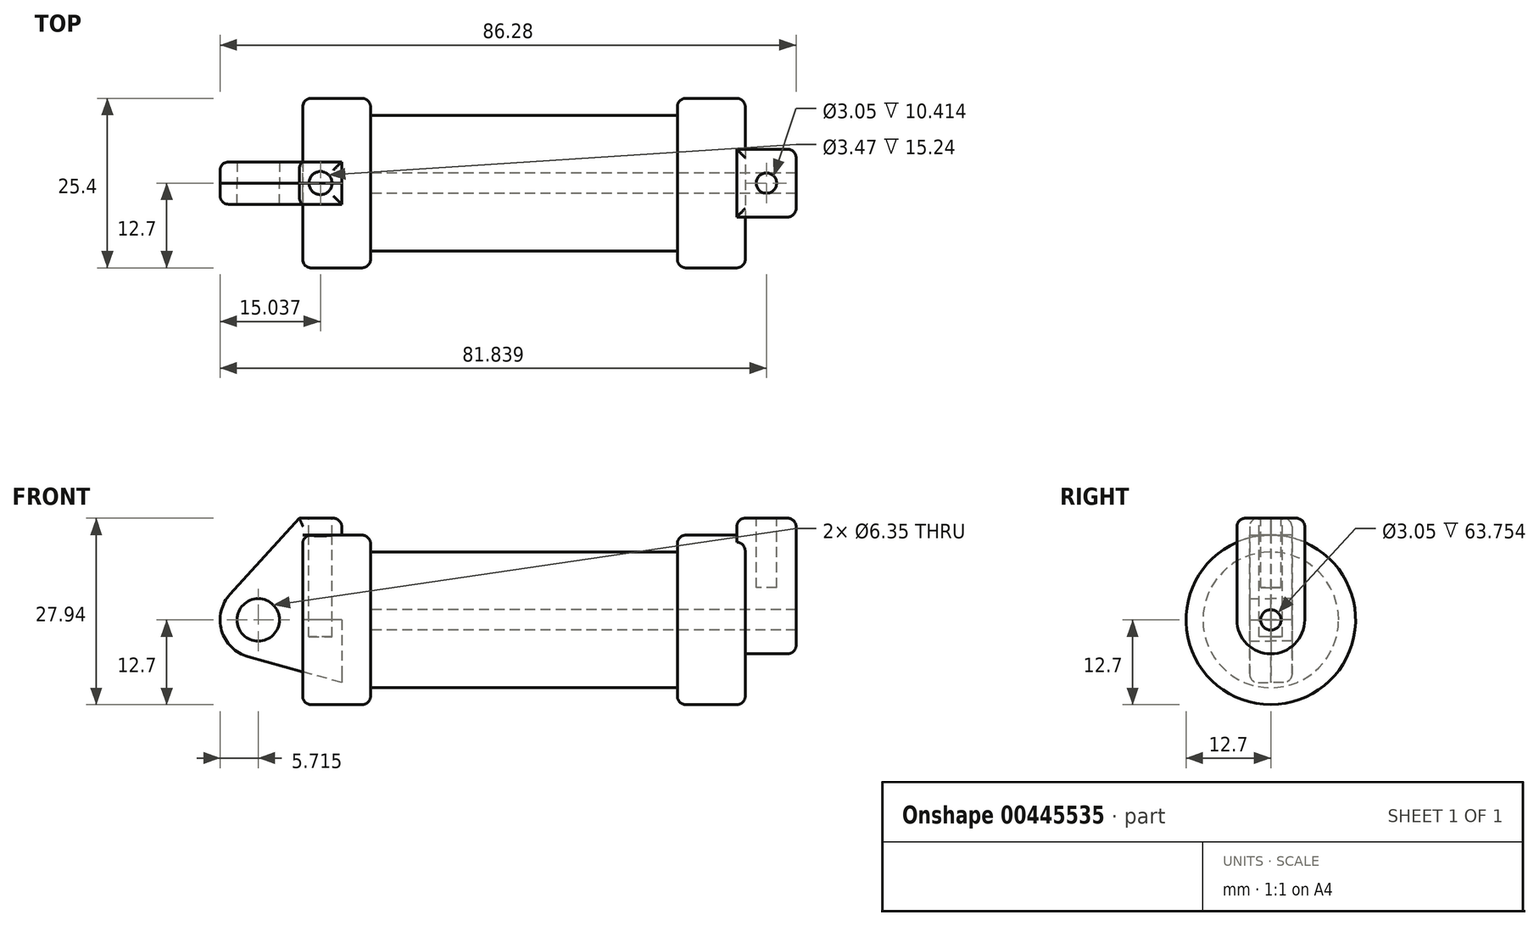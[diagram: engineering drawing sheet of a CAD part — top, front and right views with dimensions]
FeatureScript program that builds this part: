
annotation { "Feature Type Name" : "Feature", "Feature Type Description" : "" }
export const myFeature = defineFeature(function(context is Context, id is Id, definition is map)
    precondition{}
    {
        {
            var Q0;
            Q0=qCreatedBy(makeId("Front.planeOp"),FACE);
            var sketch = newSketch(context, id + "F0", { "sketchPlane" : qUnion([Q0])});
            skLineSegment(sketch, "E0", {"start": v(0, 0) * mm, "end": v(0, 12.7) * mm});
            skLineSegment(sketch, "E1", {"start": v(0, 12.7) * mm, "end": v(10.16, 12.7) * mm});
            skLineSegment(sketch, "E2", {"start": v(10.16, 12.7) * mm, "end": v(10.16, 10.16) * mm});
            skLineSegment(sketch, "E3", {"start": v(10.16, 10.16) * mm, "end": v(56.13, 10.16) * mm});
            skLineSegment(sketch, "E4", {"start": v(56.13, 10.16) * mm, "end": v(56.13, 12.7) * mm});
            skLineSegment(sketch, "E5", {"start": v(56.13, 12.7) * mm, "end": v(66.3, 12.7) * mm});
            skLineSegment(sketch, "E6", {"start": v(66.3, 12.7) * mm, "end": v(66.3, 0) * mm});
            skLineSegment(sketch, "E7", {"start": v(66.3, 0) * mm, "end": v(0, 0) * mm});
            skLineSegment(sketch, "E8", {"start": v(5.84, 15.24) * mm, "end": v(-0.5, 15.24) * mm});
            skLineSegment(sketch, "E9", {"start": v(-0.5, 15.24) * mm, "end": v(-10.88, 3.85) * mm});
            skLineSegment(sketch, "E10", {"start": v(0, 0) * mm, "end": v(-6.65, 0) * mm});
            skCircle(sketch, "E11", {"center": v(-6.65, 0) * mm, "radius": 5.72 * mm});
            skCircle(sketch, "E12", {"center": v(-6.65, 0) * mm, "radius": 3.18 * mm});
            skLineSegment(sketch, "E13", {"start": v(5.84, 15.24) * mm, "end": v(5.84, -9.4) * mm});
            skLineSegment(sketch, "E14", {"start": v(5.84, -9.4) * mm, "end": v(-8.18, -5.5) * mm});
            skSolve(sketch);
        }
        {
            var Q0;
            {var subQ0=sQuery(id+"F0.wireOp",EDGE,"E0");Q0=makeQuery(id+"F0.imprint","IMPRINT",FACE,{"disambiguationData":[TD([[makeQuery(id+"F0.imprint","IMPRINT",EDGE,{"derivedFrom":subQ0}),-1.0]])]});}
            var Q1;
            Q1=sQuery(id+"F0.wireOp",EDGE,"E7");
            revolve(context, id + "F1", {"entities" : qUnion([Q0]), "axis" : qUnion([Q1]), "revolveType" : RevolveType.FULL});
        }
        {
            var Q0;
            {var subQ0=sQuery(id+"F0.wireOp",EDGE,"E2");Q0=makeQuery(id+"F0.imprint","IMPRINT",FACE,{"disambiguationData":[TD([[makeQuery(id+"F0.imprint","IMPRINT",EDGE,{"derivedFrom":subQ0}),-1.0]])]});}
            var Q1;
            Q1=sQuery(id+"F0.wireOp",EDGE,"E7");
            revolve(context, id + "F2", {"operationType" : NewBodyOperationType.ADD, "entities" : qUnion([Q0]), "axis" : qUnion([Q1]), "revolveType" : RevolveType.FULL});
        }
        {
            var Q0;
            {var subQ5=sQuery(id+"F0.wireOp",EDGE,"E12");Q0=makeQuery(id+"F0.imprint","IMPRINT",FACE,{"disambiguationData":[TD([[makeQuery(id+"F0.imprint","IMPRINT",EDGE,{"derivedFrom":subQ5}),-1.0]])]});}
            var Q1;
            {var subQ0=sQuery(id+"F0.wireOp",EDGE,"E14");Q1=makeQuery(id+"F0.imprint","IMPRINT",FACE,{"disambiguationData":[TD([[makeQuery(id+"F0.imprint","IMPRINT",EDGE,{"derivedFrom":subQ0}),-1.0]])]});}
            var Q2;
            {var subQ1=sQuery(id+"F0.wireOp",EDGE,"E0");Q2=makeQuery(id+"F0.imprint","IMPRINT",FACE,{"disambiguationData":[TD([[makeQuery(id+"F0.imprint","IMPRINT",EDGE,{"derivedFrom":subQ1}),1.0]])]});}
            extrude(context, id + "F3", {"entities" : qUnion([Q0, Q1, Q2]), "depth" : 3.17 * mm});
        }
        {
            var Q0;
            {var subQ1=sQuery(id+"F0.wireOp",EDGE,"E0");Q0=makeQuery(id+"F0.imprint","IMPRINT",FACE,{"disambiguationData":[TD([[makeQuery(id+"F0.imprint","IMPRINT",EDGE,{"derivedFrom":subQ1}),1.0]])]});}
            var Q1;
            {var subQ5=sQuery(id+"F0.wireOp",EDGE,"E12");Q1=makeQuery(id+"F0.imprint","IMPRINT",FACE,{"disambiguationData":[TD([[makeQuery(id+"F0.imprint","IMPRINT",EDGE,{"derivedFrom":subQ5}),-1.0]])]});}
            var Q2;
            {var subQ0=sQuery(id+"F0.wireOp",EDGE,"E14");Q2=makeQuery(id+"F0.imprint","IMPRINT",FACE,{"disambiguationData":[TD([[makeQuery(id+"F0.imprint","IMPRINT",EDGE,{"derivedFrom":subQ0}),-1.0]])]});}
            extrude(context, id + "F4", {"entities" : qUnion([Q0, Q1, Q2]), "oppositeDirection" : true, "depth" : 3.17 * mm});
        }
        {
            var Q0;
            Q0=makeQuery(id+"F2.opRevolve","SWEPT_FACE",FACE,{"disambiguationData":[OSD([sQuery(id+"F0.wireOp",EDGE,"E6")])]});
            var sketch = newSketch(context, id + "F5", { "sketchPlane" : qUnion([Q0])});
            skCircle(sketch, "E15", {"center": v(0, 0) * mm, "radius": 1.52 * mm});
            skCircle(sketch, "E16", {"center": v(0, 0) * mm, "radius": 5.08 * mm});
            skLineSegment(sketch, "E17", {"start": v(-5.08, 0) * mm, "end": v(-5.08, 15.24) * mm});
            skLineSegment(sketch, "E18", {"start": v(5.08, 0) * mm, "end": v(5.08, 15.24) * mm});
            skLineSegment(sketch, "E19", {"start": v(-5.08, 15.24) * mm, "end": v(-3.2, 15.24) * mm});
            skLineSegment(sketch, "E20", {"start": v(-3.2, 15.24) * mm, "end": v(5.08, 15.24) * mm});
            skSolve(sketch);
        }
        {
            var Q0;
            Q0=qSketchRegion(id+"F5",true);
            extrude(context, id + "F6", {"entities" : qUnion([Q0]), "operationType" : NewBodyOperationType.ADD, "depth" : 7.62 * mm});
        }
        {
            var Q0;
            Q0=qSketchRegion(id+"F5",true);
            var Q1;
            Q1=makeQuery(id+"F5.imprint","IMPRINT",FACE,{"disambiguationData":[TD([[makeQuery(id+"F5.imprint","IMPRINT",EDGE,{"derivedFrom":sQuery(id+"F5.wireOp",EDGE,"E15")}),1.0]])]});
            extrude(context, id + "F7", {"entities" : qUnion([Q0, Q1]), "operationType" : NewBodyOperationType.ADD, "oppositeDirection" : true, "depth" : 1.27 * mm});
        }
        {
            var Q0;
            Q0=makeQuery(id+"F6.boolean.opBoolean","SPLIT",FACE,{"disambiguationData":[TD([makeQuery(id+"F6.opExtrude","SWEPT_FACE",FACE,{"disambiguationData":[OSD([sQuery(id+"F5.wireOp",EDGE,"E15")])]})])],"derivedFrom":makeQuery(id+"F2.opRevolve","SWEPT_FACE",FACE,{"disambiguationData":[OSD([sQuery(id+"F0.wireOp",EDGE,"E6")])]})});
            var Q1;
            Q1=makeQuery(id+"F2.opRevolve","SWEPT_FACE",FACE,{"disambiguationData":[OSD([sQuery(id+"F0.wireOp",EDGE,"E2")])]});
            extrude(context, id + "F8", {"entities" : qUnion([Q0]), "operationType" : NewBodyOperationType.REMOVE, "endBound" : BoundingType.UP_TO_SURFACE, "oppositeDirection" : true, "endBoundEntityFace" : qUnion([Q1]), "depth" : 25.4 * mm});
        }
        {
            var Q0;
            {var subQ0=sQuery(id+"F5.wireOp",EDGE,"E20");var subQ1=sQuery(id+"F5.wireOp",EDGE,"E19");Q0=makeQuery(id+"F7.boolean.opBoolean","MERGE",FACE,{"derivedFrom":[makeQuery(id+"F6.opExtrude","SWEPT_FACE",FACE,{"disambiguationData":[OSD([subQ1,subQ0])]}),makeQuery(id+"F7.opExtrude","SWEPT_FACE",FACE,{"disambiguationData":[OSD([subQ1,subQ0])]})]});}
            var sketch = newSketch(context, id + "F9", { "sketchPlane" : qUnion([Q0])});
            skLineSegment(sketch, "E21", {"start": v(69.47, 5.08) * mm, "end": v(69.47, -5.08) * mm, "construction": true});
            skLineSegment(sketch, "E22", {"start": v(73.91, 0) * mm, "end": v(65.02, 0) * mm, "construction": true});
            skCircle(sketch, "E23", {"center": v(69.47, 0) * mm, "radius": 1.52 * mm});
            skSolve(sketch);
        }
        {
            var Q0;
            Q0=makeQuery(id+"F9.imprint","IMPRINT",FACE,{"disambiguationData":[TD([[makeQuery(id+"F9.imprint","IMPRINT",EDGE,{"derivedFrom":sQuery(id+"F9.wireOp",EDGE,"E23")}),1.0]])]});
            extrude(context, id + "F10", {"entities" : qUnion([Q0]), "operationType" : NewBodyOperationType.REMOVE, "oppositeDirection" : true, "depth" : 10.4 * mm});
        }
        {
            var Q0;
            Q0=makeQuery(id+"F4.opExtrude","SWEPT_FACE",FACE,{"disambiguationData":[OSD([sQuery(id+"F0.wireOp",EDGE,"E8")])]});
            var sketch = newSketch(context, id + "F11", { "sketchPlane" : qUnion([Q0])});
            skCircle(sketch, "E24", {"center": v(2.67, 0) * mm, "radius": 1.73 * mm});
            skSolve(sketch);
        }
        {
            var Q0;
            {var subQ0=sQuery(id+"F11.wireOp",EDGE,"E24");var subQ1=makeQuery(id+"F4.opExtrude","CAP_EDGE",EDGE,{"disambiguationData":[OSD([sQuery(id+"F0.wireOp",EDGE,"E8")])],"isStart":true});var subQ2=makeQuery(id+"F11.imprint","INTERSECT",VERTEX,{"disambiguationData":[OD(0.0)],"derivedFrom":[subQ1,subQ0]});Q0=makeQuery(id+"F11.imprint","IMPRINT",FACE,{"disambiguationData":[TD([[makeQuery(id+"F11.imprint","IMPRINT",EDGE,{"disambiguationData":[TD([[subQ2,-1.0]])],"derivedFrom":subQ0}),1.0]])]});}
            var Q1;
            {var subQ0=sQuery(id+"F11.wireOp",EDGE,"E24");var subQ1=makeQuery(id+"F4.opExtrude","CAP_EDGE",EDGE,{"disambiguationData":[OSD([sQuery(id+"F0.wireOp",EDGE,"E8")])],"isStart":true});var subQ2=makeQuery(id+"F11.imprint","INTERSECT",VERTEX,{"disambiguationData":[OD(0.0)],"derivedFrom":[subQ1,subQ0]});Q1=makeQuery(id+"F11.imprint","IMPRINT",FACE,{"disambiguationData":[TD([[makeQuery(id+"F11.imprint","IMPRINT",EDGE,{"disambiguationData":[TD([[subQ2,1.0]])],"derivedFrom":subQ0}),1.0]])]});}
            extrude(context, id + "F12", {"entities" : qUnion([Q0, Q1]), "operationType" : NewBodyOperationType.REMOVE, "oppositeDirection" : true, "depth" : 17.78 * mm});
        }
        {
            var Q0;
            {var subQ0=sQuery(id+"F11.wireOp",EDGE,"E24");var subQ1=makeQuery(id+"F4.opExtrude","CAP_EDGE",EDGE,{"disambiguationData":[OSD([sQuery(id+"F0.wireOp",EDGE,"E8")])],"isStart":true});var subQ2=makeQuery(id+"F11.imprint","INTERSECT",VERTEX,{"disambiguationData":[OD(0.0)],"derivedFrom":[subQ1,subQ0]});Q0=makeQuery(id+"F11.imprint","IMPRINT",FACE,{"disambiguationData":[TD([[makeQuery(id+"F11.imprint","IMPRINT",EDGE,{"disambiguationData":[TD([[subQ2,1.0]])],"derivedFrom":subQ0}),1.0]])]});}
            extrude(context, id + "F13", {"entities" : qUnion([Q0]), "operationType" : NewBodyOperationType.REMOVE, "oppositeDirection" : true, "depth" : 17.78 * mm});
        }
        {
            var Q0;
            Q0=makeQuery(id+"F2.opRevolve","SWEPT_EDGE",EDGE,{"disambiguationData":[OSD([sQuery(id+"F0.wireOp",EDGE,"E1"),sQuery(id+"F0.wireOp",EDGE,"E2")])]});
            fillet(context, id + "F14", {"entities" : qUnion([Q0]), "radius" : 1.27 * mm, "tangentPropagation" : true, "allowEdgeOverflow" : false});
        }
        {
            var Q0;
            {var subQ0=sQuery(id+"F0.wireOp",EDGE,"E5");var subQ1=sQuery(id+"F0.wireOp",EDGE,"E6");Q0=makeQuery(id+"F6.boolean.opBoolean","SPLIT",EDGE,{"disambiguationData":[topologyDisambiguationEdgeConnected([makeQuery(id+"F2.opRevolve","SWEPT_FACE",FACE,{"disambiguationData":[OSD([subQ1])]})])],"derivedFrom":makeQuery(id+"F2.opRevolve","SWEPT_EDGE",EDGE,{"disambiguationData":[OSD([subQ0,subQ1])]})});}
            var Q1;
            Q1=makeQuery(id+"F6.opExtrude","CAP_EDGE",EDGE,{"disambiguationData":[OSD([sQuery(id+"F5.wireOp",EDGE,"E19"),sQuery(id+"F5.wireOp",EDGE,"E20")])],"isStart":false});
            var Q2;
            Q2=makeQuery(id+"F3.opExtrude","CAP_EDGE",EDGE,{"disambiguationData":[OSD([sQuery(id+"F0.wireOp",EDGE,"E8")])],"isStart":false});
            var Q3;
            Q3=makeQuery(id+"F4.opExtrude","CAP_EDGE",EDGE,{"disambiguationData":[OSD([sQuery(id+"F0.wireOp",EDGE,"E8")])],"isStart":false});
            var Q4;
            Q4=makeQuery(id+"F4.opExtrude","SWEPT_EDGE",EDGE,{"disambiguationData":[OSD([sQuery(id+"F0.wireOp",EDGE,"E8"),sQuery(id+"F0.wireOp",EDGE,"E13")])]});
            var Q5;
            Q5=makeQuery(id+"F2.opRevolve","SWEPT_EDGE",EDGE,{"disambiguationData":[OSD([sQuery(id+"F0.wireOp",EDGE,"E4"),sQuery(id+"F0.wireOp",EDGE,"E5")])]});
            var Q6;
            Q6=makeQuery(id+"F3.opExtrude","SWEPT_EDGE",EDGE,{"disambiguationData":[OSD([sQuery(id+"F0.wireOp",EDGE,"E8"),sQuery(id+"F0.wireOp",EDGE,"E13")])]});
            var Q7;
            Q7=makeQuery(id+"F1.opRevolve","SWEPT_EDGE",EDGE,{"disambiguationData":[OSD([sQuery(id+"F0.wireOp",EDGE,"E0"),sQuery(id+"F0.wireOp",EDGE,"E1")])]});
            var Q8;
            {var subQ0=sQuery(id+"F5.wireOp",EDGE,"E19");var subQ1=sQuery(id+"F5.wireOp",EDGE,"E17");Q8=makeQuery(id+"F7.boolean.opBoolean","MERGE",EDGE,{"derivedFrom":[makeQuery(id+"F6.opExtrude","SWEPT_EDGE",EDGE,{"disambiguationData":[OSD([subQ1,subQ0])]}),makeQuery(id+"F7.opExtrude","SWEPT_EDGE",EDGE,{"disambiguationData":[OSD([subQ1,subQ0])]})]});}
            var Q9;
            Q9=makeQuery(id+"F7.opExtrude","CAP_EDGE",EDGE,{"disambiguationData":[OSD([sQuery(id+"F5.wireOp",EDGE,"E19"),sQuery(id+"F5.wireOp",EDGE,"E20")])],"isStart":false});
            var Q10;
            {var subQ0=sQuery(id+"F5.wireOp",EDGE,"E20");var subQ1=sQuery(id+"F5.wireOp",EDGE,"E18");Q10=makeQuery(id+"F7.boolean.opBoolean","MERGE",EDGE,{"derivedFrom":[makeQuery(id+"F6.opExtrude","SWEPT_EDGE",EDGE,{"disambiguationData":[OSD([subQ1,subQ0])]}),makeQuery(id+"F7.opExtrude","SWEPT_EDGE",EDGE,{"disambiguationData":[OSD([subQ1,subQ0])]})]});}
            var Q11;
            Q11=makeQuery(id+"F4.opExtrude","CAP_EDGE",EDGE,{"disambiguationData":[OSD([sQuery(id+"F0.wireOp",EDGE,"E9")])],"isStart":false});
            var Q12;
            Q12=makeQuery(id+"F3.opExtrude","CAP_EDGE",EDGE,{"disambiguationData":[OSD([sQuery(id+"F0.wireOp",EDGE,"E11")])],"isStart":false});
            var Q13;
            Q13=makeQuery(id+"F6.opExtrude","CAP_EDGE",EDGE,{"disambiguationData":[OSD([sQuery(id+"F5.wireOp",EDGE,"E17")])],"isStart":false});
            fillet(context, id + "F15", {"entities" : qUnion([Q0, Q1, Q2, Q3, Q4, Q5, Q6, Q7, Q8, Q9, Q10, Q11, Q12, Q13]), "radius" : 1.27 * mm, "tangentPropagation" : true, "allowEdgeOverflow" : false});
        }
    });
